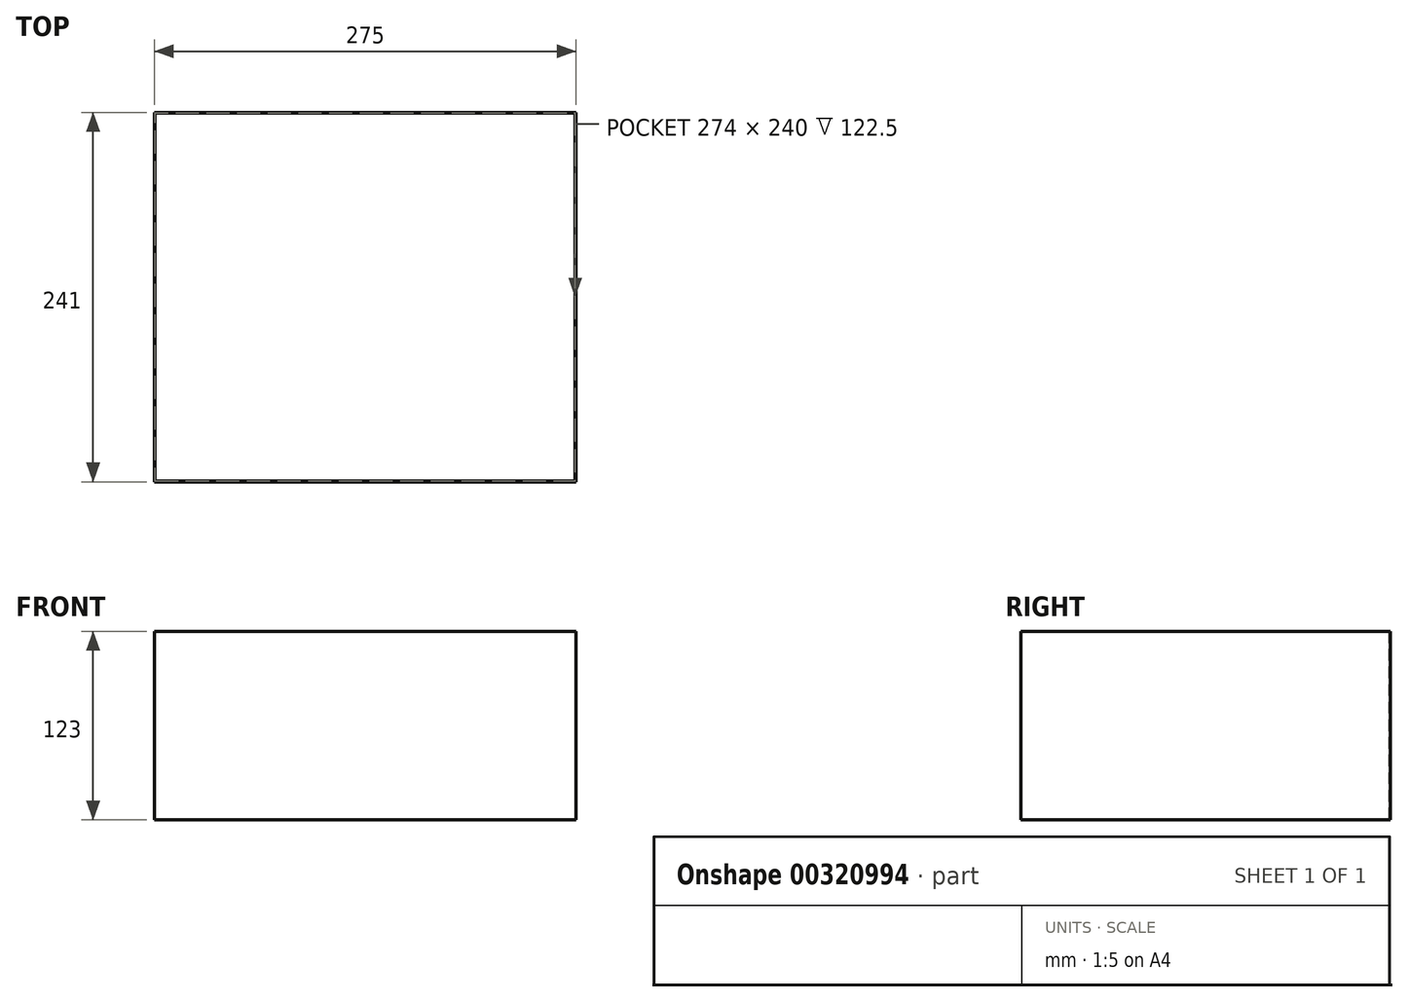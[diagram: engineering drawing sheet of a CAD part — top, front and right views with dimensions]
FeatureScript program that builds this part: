
annotation { "Feature Type Name" : "Feature", "Feature Type Description" : "" }
export const myFeature = defineFeature(function(context is Context, id is Id, definition is map)
    precondition{}
    {
        {
            var Q0;
            Q0=qCreatedBy(makeId("Front.planeOp"),FACE);
            var sketch = newSketch(context, id + "F0", { "sketchPlane" : qUnion([Q0])});
            skLineSegment(sketch, "E0", {"start": v(0, 0) * mm, "end": v(0, 123) * mm});
            skLineSegment(sketch, "E1", {"start": v(0, 123) * mm, "end": v(275, 123) * mm});
            skLineSegment(sketch, "E2", {"start": v(275, 123) * mm, "end": v(275, 0) * mm});
            skLineSegment(sketch, "E3", {"start": v(275, 0) * mm, "end": v(0, 0) * mm});
            skSolve(sketch);
        }
        {
            var Q0;
            Q0 = qSketchRegion(id + "F0", true);
            extrude(context, id + "F1", {"entities" : qUnion([Q0]), "depth" : 241 * mm});
        }
        {
            var Q0;
            Q0=makeQuery(id+"F1.opExtrude","SWEPT_FACE",FACE,{"disambiguationData":[OSD([sQuery(id+"F0.wireOp",EDGE,"E1")])]});
            shell(context, id + "F2", {"entities" : qUnion([Q0]), "thickness" : .5 * mm});
        }
    });
